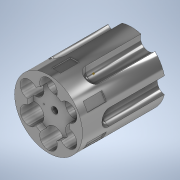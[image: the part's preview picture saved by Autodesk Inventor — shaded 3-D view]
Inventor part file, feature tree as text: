
AUTODESK INVENTOR PART (.ipt)
format: ipt  version: 2021 (Build 250183000, 183)  size: 291,328 bytes
history: native  units: mm
features: sketch x10, extrude x9, other x7, pattern_circular x4
ambient origin geometry x8: Origin, YZ Plane, XZ Plane, XY Plane, X Axis, Y Axis, Z Axis, Center Point
bodies: Body1 (feature_tree)
feature tree (30):
  other  "Baril do revólver"
  other  "Sólido1"
  extrude  "Extrusão1"  Depth=33.0mm TaperAngle=0.0deg
  sketch  "Esboço2"  dims[d3=6.5mm d4=7.0mm]
  extrude  "Extrusão2"  Depth=7.0mm
  pattern_circular  "Padrão circular1"  Count=6 Angle=360.0deg
  extrude  "Extrusão3"  Depth=0.5mm
  sketch  "Esboço6"  dims[d11=6.5mm d12=0.5mm]
  other  "Ponto de trabalho1"
  other  "Revolução1"
  pattern_circular  "Padrão circular2"  Count=6 Angle=360.0deg
  other  "Plano de trabalho2"
  extrude  "Extrusão4"  Depth=7.5mm
  pattern_circular  "Padrão circular3"  [2 undecoded]
  extrude  "Extrusão5"  Depth=5.0mm TaperAngle=360.0deg
  other  "Plano de trabalho3"
  extrude  "Extrusão6"  Depth=3.0mm TaperAngle=0.0deg
  pattern_circular  "Padrão circular4"  [2 undecoded]
  extrude  "Extrusão7"  Depth=5.0mm
  extrude  "Extrusão8"  Depth=5.0mm
  extrude  "Extrusão9"  Depth=5.0mm
  sketch  "Esboço1"  dims[d0=27.0mm d1=33.0mm d2=0.0mm]
  sketch  "Esboço3"  dims[d5=9.0mm]
  sketch  "Esboço4"  dims[d6=0.0mm d7=0.0mm d8=60.0mm d9=360.0deg]
  other  "Contorno projetado1"
  sketch  "Esboço7"  dims[d13=22.0mm d14=0.0mm]
  sketch  "Esboço8"  dims[d15=90.0deg d16=60.0mm d17=360.0deg]
  sketch  "Esboço9"  dims[d19=13.0mm d20=7.5mm]
  sketch  "Esboço10"  dims[d21=3.5mm]
  sketch  "Esboço11"  dims[d22=3.0mm d23=1.0mm d24=0.0mm d25=60.0mm d26=360.0deg d28=3.0mm d29=0.0mm d30=3.25mm d33=3.281864mm d34=2.191261mm d35=0.408292mm d36=3.0mm d37=0.0mm d38=60.0mm d39=360.0deg d41=2.5mm d42=0.0mm d43=0.0mm d44=16.7mm d45=10.0mm d46=2.5mm d47=0.0mm d48=0.0mm d49=0.5mm d50=4.3mm d51=5.0mm d52=0.0mm]
note: 4 required parameter values undecoded (feature->parameter linkage not recoverable at this tier; creation-order binding heuristic only, values carry confidence <= 0.55)
